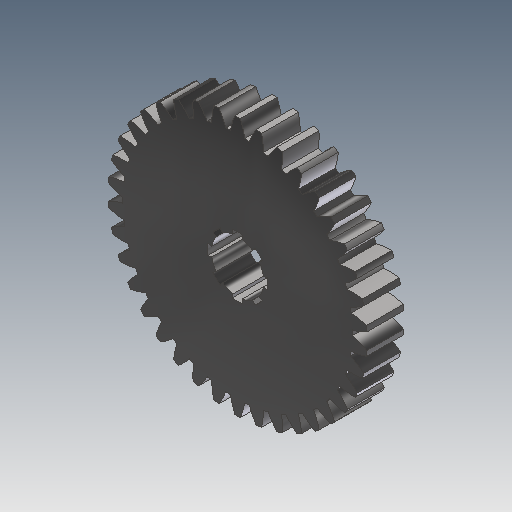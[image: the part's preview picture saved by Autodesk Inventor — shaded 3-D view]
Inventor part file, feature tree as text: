
AUTODESK INVENTOR PART (.ipt)
format: ipt  version: 2017 (Build 210142000, 142)  size: 351,232 bytes
history: native  units: mm (DEFAULTED — no unit token found)
features: extrude x3, plane x3, other x3, sketch x2, pattern_circular x1
ambient origin geometry x8: Origin, YZ Plane, XZ Plane, XY Plane, X Axis, Y Axis, Z Axis, Center Point
bodies: Solid1 (feature_tree)
feature tree (12):
  extrude  "Extrusion1"  Depth=1.4mm TaperAngle=0.0deg
  plane  "Work Plane2"
  plane  "Work Plane8"
  plane  "Work Plane9"
  other  "Цилиндрическое зубчатое зацепление"
  sketch  "Эскиз3"
  extrude  "Выдавливание2"  Depth=10.0mm
  extrude  "Выдавливание3"  Depth=10.0mm TaperAngle=0.0deg
  pattern_circular  "Круговой массив1"  [2 undecoded]
  sketch  "Sketch2"  dims[d0=9.865mm d1=1.4mm d2=0.0mm d3=9.5mm d4=10.0mm d5=0.0mm d16=6.0mm d17=0.0mm d34=0.826735mm d39=0.0mm d41=0.0mm d43=6.0mm d46=6.0mm d47=0.0mm d48=0.0mm d49=2.0mm d50=0.15mm d51=3.490659mm d52=10.0mm d53=0.0mm d54=10.0mm d55=0.0mm d56=80.0mm d57=360.0deg]
  other  "Srf1"
  other  "Средний диаметр"
note: 2 required parameter values undecoded (feature->parameter linkage not recoverable at this tier; creation-order binding heuristic only, values carry confidence <= 0.55)
